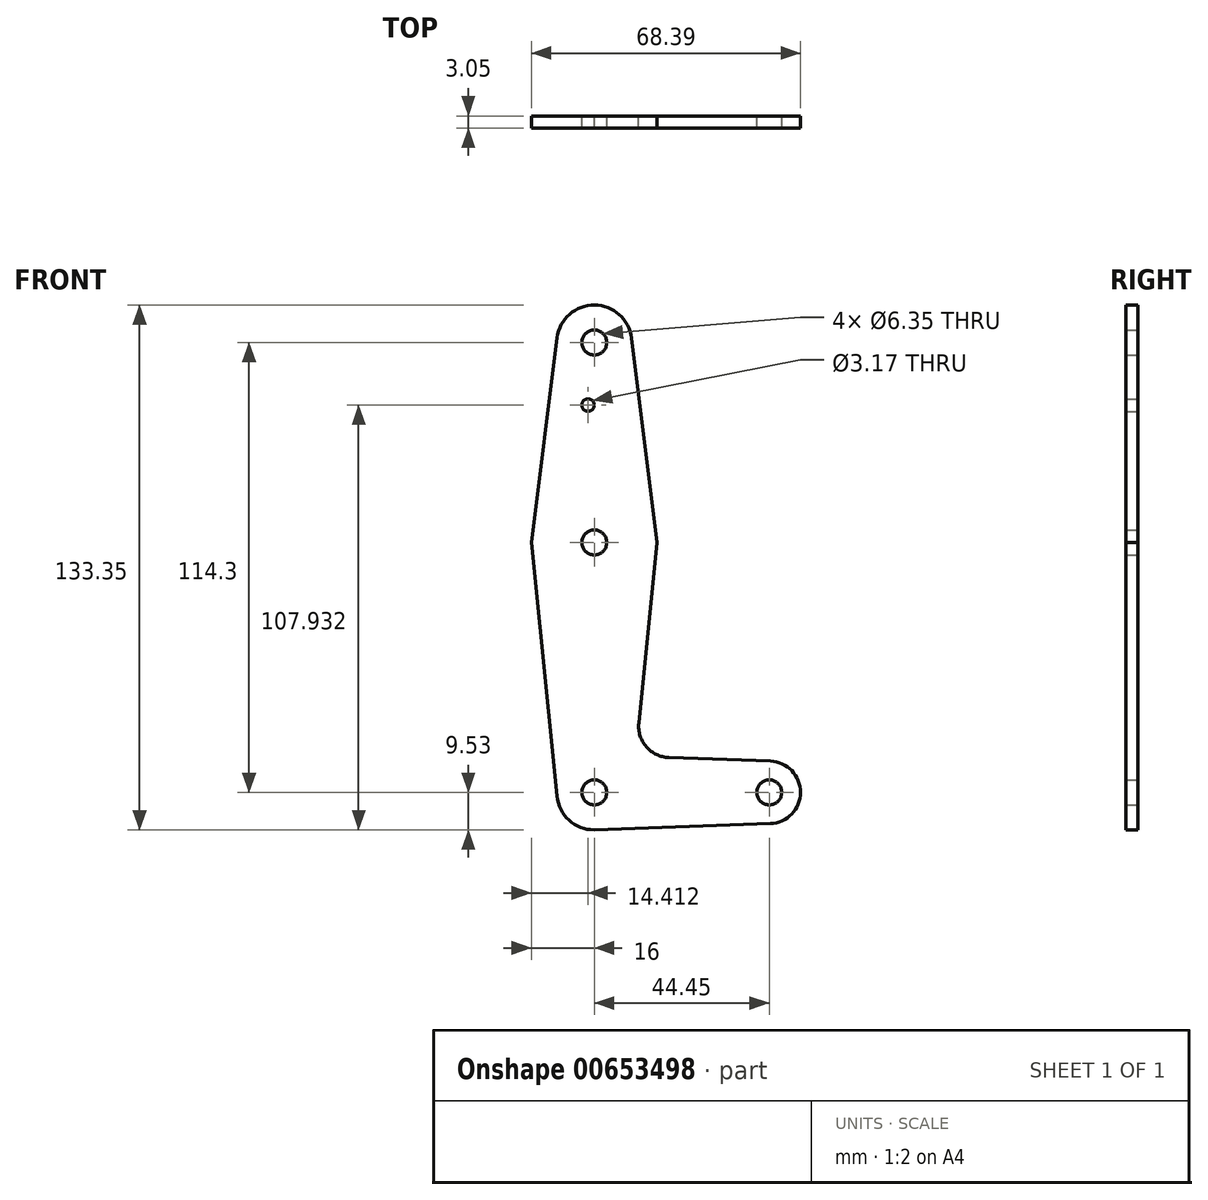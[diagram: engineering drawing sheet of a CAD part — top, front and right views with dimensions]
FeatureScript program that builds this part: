
annotation { "Feature Type Name" : "Feature", "Feature Type Description" : "" }
export const myFeature = defineFeature(function(context is Context, id is Id, definition is map)
    precondition{}
    {
        {
            var Q0;
            Q0=qCreatedBy(makeId("Front.planeOp"),FACE);
            var sketch = newSketch(context, id + "F0", { "sketchPlane" : qUnion([Q0])});
            skCircle(sketch, "E0", {"center": v(0, 0) * mm, "radius": 15.88 * mm});
            skCircle(sketch, "E1", {"center": v(0, 50.8) * mm, "radius": 9.53 * mm});
            skCircle(sketch, "E2", {"center": v(0, -63.5) * mm, "radius": 9.53 * mm});
            skCircle(sketch, "E3", {"center": v(44.45, -63.5) * mm, "radius": 7.94 * mm});
            skLineSegment(sketch, "E4", {"start": v(0, 50.8) * mm, "end": v(0, 0) * mm, "construction": true});
            skLineSegment(sketch, "E5", {"start": v(0, -63.5) * mm, "end": v(0, 0) * mm, "construction": true});
            skLineSegment(sketch, "E6", {"start": v(0, -63.5) * mm, "end": v(44.45, -63.5) * mm, "construction": true});
            skCircle(sketch, "E7", {"center": v(0, 50.8) * mm, "radius": 3.18 * mm});
            skCircle(sketch, "E8", {"center": v(0, 0) * mm, "radius": 3.18 * mm});
            skCircle(sketch, "E9", {"center": v(0, -63.5) * mm, "radius": 3.18 * mm});
            skCircle(sketch, "E10", {"center": v(44.45, -63.5) * mm, "radius": 3.18 * mm});
            skLineSegment(sketch, "E11", {"start": v(-9.45, 52) * mm, "end": v(-16, 0) * mm});
            skLineSegment(sketch, "E12", {"start": v(-16, 0) * mm, "end": v(-9.48, -64.46) * mm});
            skLineSegment(sketch, "E13", {"start": v(15.88, 0) * mm, "end": v(11.32, -45.92) * mm});
            skCircle(sketch, "E14", {"center": v(-1.59, 34.9) * mm, "radius": 1.59 * mm});
            skLineSegment(sketch, "E15", {"start": v(0, -73.03) * mm, "end": v(44.73, -71.43) * mm});
            skPoint(sketch, "E16.newPointA", {"position": v(9.48, -64.46) * mm});
            skArc(sketch, "E16.filletArc", {"start": v(11.32, -45.92) * mm, "mid": v(13.24, -51.93) * mm, "end": v(18.94, -54.65) * mm});
            skLineSegment(sketch, "E17", {"start": v(9.45, 51.97) * mm, "end": v(15.88, 0) * mm});
            skLineSegment(sketch, "E18", {"start": v(18.94, -54.65) * mm, "end": v(44.73, -55.57) * mm});
            skSolve(sketch);
        }
        {
            var Q0;
            Q0=makeQuery(id+"F0.imprint","IMPRINT",FACE,{"disambiguationData":[TD([[makeQuery(id+"F0.imprint","IMPRINT",EDGE,{"derivedFrom":sQuery(id+"F0.wireOp",EDGE,"E7")}),-1.0]])]});
            var Q1;
            Q1=makeQuery(id+"F0.imprint","IMPRINT",FACE,{"disambiguationData":[TD([[makeQuery(id+"F0.imprint","IMPRINT",EDGE,{"derivedFrom":sQuery(id+"F0.wireOp",EDGE,"E14")}),-1.0]])]});
            var Q2;
            Q2=makeQuery(id+"F0.imprint","IMPRINT",FACE,{"disambiguationData":[TD([[makeQuery(id+"F0.imprint","IMPRINT",EDGE,{"derivedFrom":sQuery(id+"F0.wireOp",EDGE,"E8")}),-1.0]])]});
            var Q3;
            {var subQ8=sQuery(id+"F0.wireOp",EDGE,"E12");Q3=makeQuery(id+"F0.imprint","IMPRINT",FACE,{"disambiguationData":[TD([[makeQuery(id+"F0.imprint","IMPRINT",EDGE,{"derivedFrom":subQ8}),1.0]])]});}
            var Q4;
            Q4=makeQuery(id+"F0.imprint","IMPRINT",FACE,{"disambiguationData":[TD([[makeQuery(id+"F0.imprint","IMPRINT",EDGE,{"derivedFrom":sQuery(id+"F0.wireOp",EDGE,"E9")}),-1.0]])]});
            var Q5;
            Q5=makeQuery(id+"F0.imprint","IMPRINT",FACE,{"disambiguationData":[TD([[makeQuery(id+"F0.imprint","IMPRINT",EDGE,{"derivedFrom":sQuery(id+"F0.wireOp",EDGE,"E10")}),-1.0]])]});
            extrude(context, id + "F1", {"entities" : qUnion([Q0, Q1, Q2, Q3, Q4, Q5]), "depth" : 3.05 * mm, "offsetDistance" : 25.4 * mm});
        }
    });
